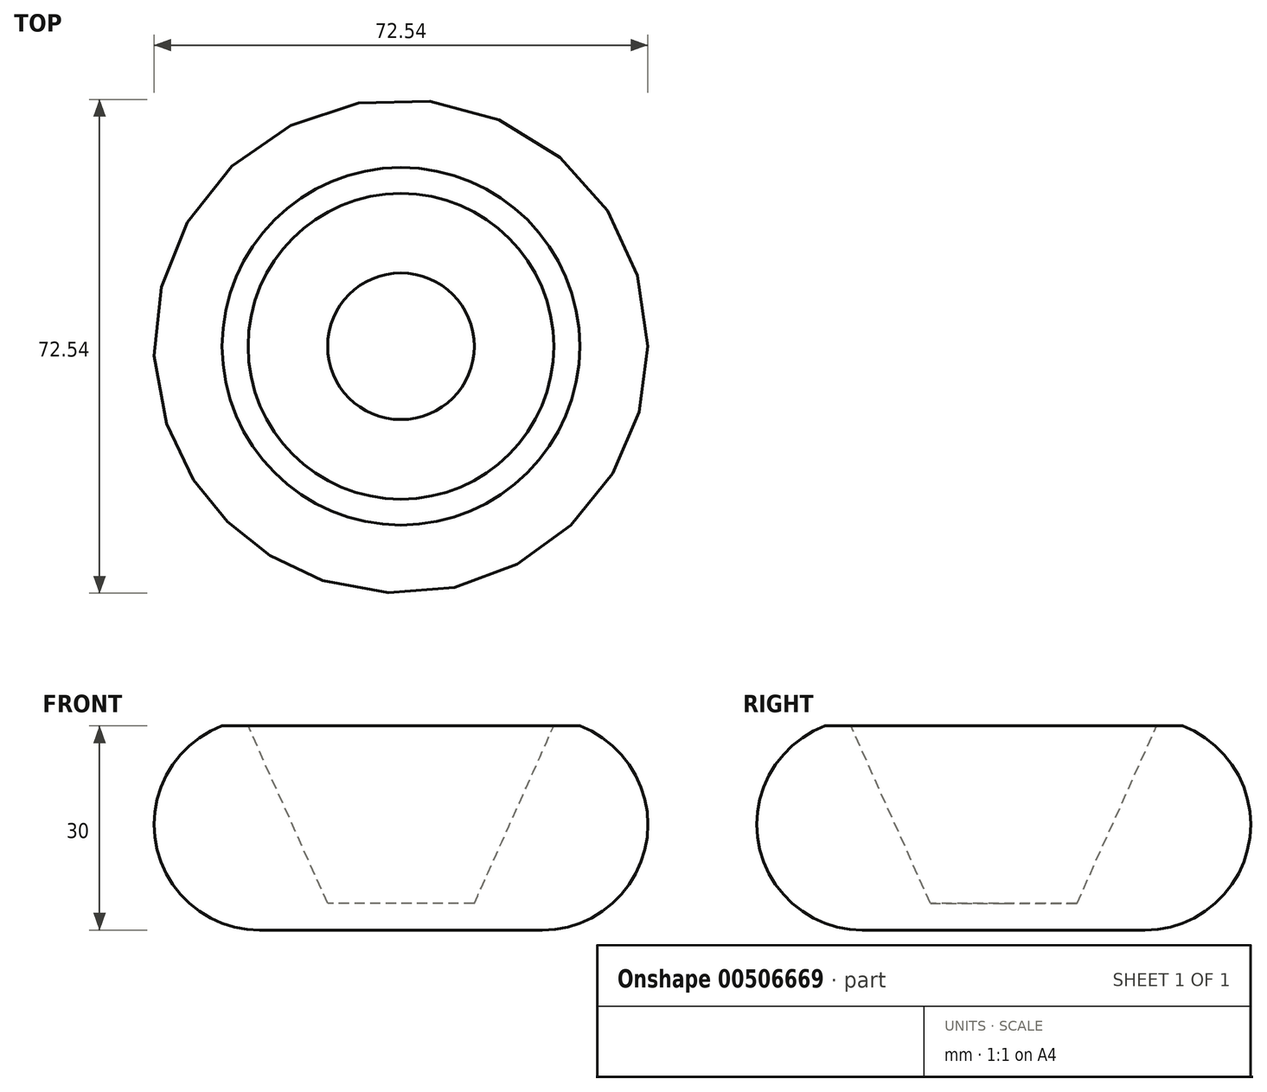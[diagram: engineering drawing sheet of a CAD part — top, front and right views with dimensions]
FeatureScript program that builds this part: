
annotation { "Feature Type Name" : "Feature", "Feature Type Description" : "" }
export const myFeature = defineFeature(function(context is Context, id is Id, definition is map)
    precondition{}
    {
        {
            var Q0;
            Q0=qCreatedBy(makeId("Front.planeOp"),FACE);
            var sketch = newSketch(context, id + "F0", { "sketchPlane" : qUnion([Q0])});
            skLineSegment(sketch, "E0", {"start": v(0, 0) * mm, "end": v(10, 0) * mm});
            skLineSegment(sketch, "E1", {"start": v(15.5, 30) * mm, "end": v(11.68, 30) * mm});
            skLineSegment(sketch, "E2", {"start": v(11.68, 30) * mm, "end": v(0, 3.93) * mm});
            skLineSegment(sketch, "E3", {"start": v(0, 3.93) * mm, "end": v(-10.77, 3.93) * mm});
            skLineSegment(sketch, "E4", {"start": v(-10.77, 3.93) * mm, "end": v(-10.77, 0) * mm});
            skLineSegment(sketch, "E5", {"start": v(-10.77, 0) * mm, "end": v(0, 0) * mm});
            skArc(sketch, "E6", {"start": v(10, 0) * mm, "mid": v(25.25, 12.7) * mm, "end": v(15.5, 30) * mm});
            skSolve(sketch);
        }
        {
            var Q0;
            Q0=makeQuery(id+"F0.imprint","IMPRINT",FACE,{"disambiguationData":[TD([[makeQuery(id+"F0.imprint","IMPRINT",EDGE,{"derivedFrom":sQuery(id+"F0.wireOp",EDGE,"E0")}),1.0]])]});
            var Q1;
            Q1=sQuery(id+"F0.wireOp",EDGE,"E4");
            revolve(context, id + "F1", {"entities" : qUnion([Q0]), "axis" : qUnion([Q1]), "revolveType" : RevolveType.FULL});
        }
    });
